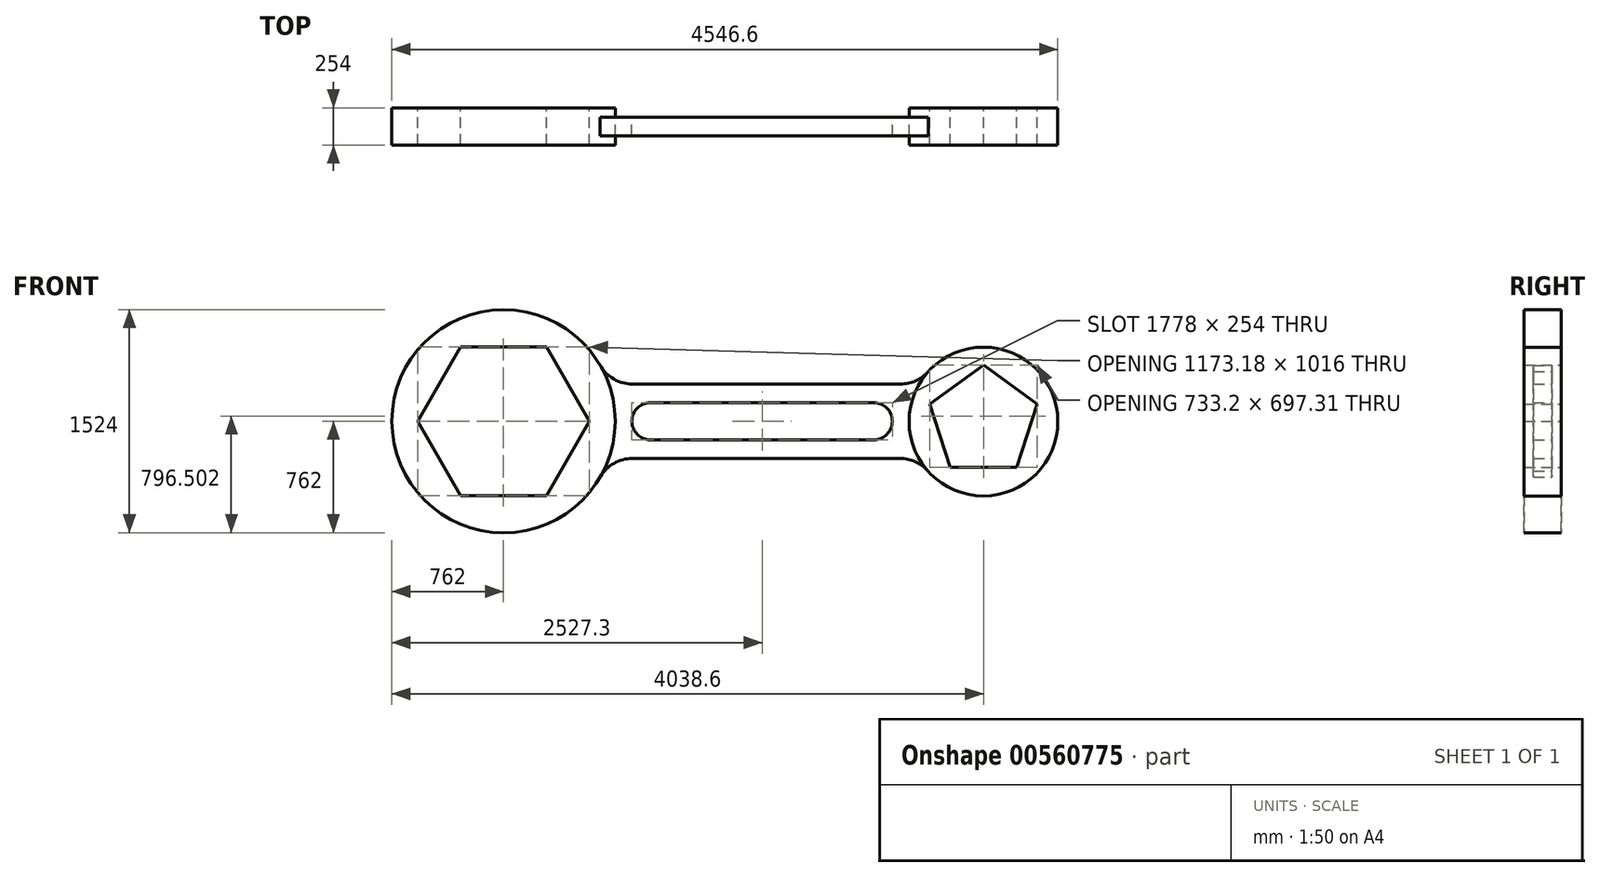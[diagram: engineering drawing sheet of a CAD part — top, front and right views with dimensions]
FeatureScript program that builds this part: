
annotation { "Feature Type Name" : "Feature", "Feature Type Description" : "" }
export const myFeature = defineFeature(function(context is Context, id is Id, definition is map)
    precondition{}
    {
        {
            var Q0;
            Q0=qCreatedBy(makeId("Front.planeOp"),FACE);
            var sketch = newSketch(context, id + "F0", { "sketchPlane" : qUnion([Q0])});
            skLineSegment(sketch, "E0", {"start": v(0, 0) * mm, "end": v(1524, 0) * mm});
            skLineSegment(sketch, "E1", {"start": v(0, 254) * mm, "end": v(1524, 254) * mm});
            skArc(sketch, "E2", {"start": v(0, 254) * mm, "mid": v(-127, 127) * mm, "end": v(0, 0) * mm});
            skArc(sketch, "E3", {"start": v(1524, 0) * mm, "mid": v(1651, 127) * mm, "end": v(1524, 254) * mm});
            skPoint(sketch, "E4.centerSnap0", {"position": v(1651, 127) * mm});
            skPoint(sketch, "E5.0.midPoint", {"position": v(-622.3, -127) * mm});
            skPoint(sketch, "E6.0.midPoint", {"position": v(2019.3, -63.5) * mm});
            skPoint(sketch, "E7.centerSnap0", {"position": v(-127, 127) * mm});
            skCircle(sketch, "E8", {"center": v(-1003.3, 127) * mm, "radius": 762 * mm});
            skLineSegment(sketch, "E9.0", {"start": v(-710, -381) * mm, "end": v(-1296.6, -381) * mm});
            skLineSegment(sketch, "E9.1", {"start": v(-1296.6, -381) * mm, "end": v(-1589.89, 127) * mm});
            skLineSegment(sketch, "E9.2", {"start": v(-1589.89, 127) * mm, "end": v(-1296.6, 635) * mm});
            skLineSegment(sketch, "E9.3", {"start": v(-1296.6, 635) * mm, "end": v(-710, 635) * mm});
            skLineSegment(sketch, "E9.4", {"start": v(-710, 635) * mm, "end": v(-416.71, 127) * mm});
            skLineSegment(sketch, "E9.5", {"start": v(-416.71, 127) * mm, "end": v(-710, -381) * mm});
            skPoint(sketch, "E9.0.midPoint", {"position": v(-1003.3, -381) * mm});
            skArc(sketch, "E10", {"start": v(2279.5, 505.64) * mm, "mid": v(2273.3, 505.7) * mm, "end": v(2267.08, 505.64) * mm});
            skLineSegment(sketch, "E11.0", {"start": v(2499.87, -187.15) * mm, "end": v(2046.73, -187.15) * mm});
            skLineSegment(sketch, "E11.1", {"start": v(2046.73, -187.15) * mm, "end": v(1906.7, 243.8) * mm});
            skLineSegment(sketch, "E11.2", {"start": v(1906.7, 243.8) * mm, "end": v(2273.3, 510.16) * mm});
            skLineSegment(sketch, "E11.3", {"start": v(2273.3, 510.16) * mm, "end": v(2639.9, 243.8) * mm});
            skLineSegment(sketch, "E11.4", {"start": v(2639.9, 243.8) * mm, "end": v(2499.87, -187.15) * mm});
            skPoint(sketch, "E11.0.midPoint", {"position": v(2273.3, -187.15) * mm});
            skArc(sketch, "E12.trimOffspring", {"start": v(1912.91, 248.32) * mm, "mid": v(1910.94, 242.43) * mm, "end": v(1909.07, 236.5) * mm});
            skArc(sketch, "E13.trimOffspring", {"start": v(2044.35, -179.85) * mm, "mid": v(2049.35, -183.54) * mm, "end": v(2054.4, -187.15) * mm});
            skArc(sketch, "E14.trimOffspring", {"start": v(2492.18, -187.15) * mm, "mid": v(2497.24, -183.54) * mm, "end": v(2502.24, -179.85) * mm});
            skArc(sketch, "E15.trimOffspring", {"start": v(2637.52, 236.5) * mm, "mid": v(2635.65, 242.43) * mm, "end": v(2633.68, 248.32) * mm});
            skPoint(sketch, "E16.start.orphan", {"position": v(0, -127) * mm});
            skPoint(sketch, "E17.start.orphan", {"position": v(0, 381) * mm});
            skLineSegment(sketch, "E18", {"start": v(-127, -127) * mm, "end": v(1651, -127) * mm});
            skLineSegment(sketch, "E19", {"start": v(-127, 381) * mm, "end": v(1651, 381) * mm});
            skArc(sketch, "E20", {"start": v(-123.42, -127) * mm, "mid": v(-250.42, -161.03) * mm, "end": v(-343.39, -254) * mm});
            skArc(sketch, "E21", {"start": v(-343.39, 508) * mm, "mid": v(-250.42, 415.03) * mm, "end": v(-123.42, 381) * mm});
            skCircle(sketch, "E22", {"center": v(2273.3, 124.7) * mm, "radius": 508 * mm});
            skArc(sketch, "E23", {"start": v(1893.29, -212.44) * mm, "mid": v(1807.44, -149.34) * mm, "end": v(1703.28, -127) * mm});
            skArc(sketch, "E24", {"start": v(1707.4, 381) * mm, "mid": v(1810.63, 402.92) * mm, "end": v(1896.04, 464.9) * mm});
            skLineSegment(sketch, "E25", {"start": v(1651, 381) * mm, "end": v(1707.4, 381) * mm});
            skLineSegment(sketch, "E26", {"start": v(1651, -127) * mm, "end": v(1703.28, -127) * mm});
            skLineSegment(sketch, "E27.trimOffspring", {"start": v(1834.7, 381) * mm, "end": v(1849.9, 381) * mm});
            skSolve(sketch);
        }
        {
            var Q0;
            Q0=makeQuery(id+"F0.imprint","IMPRINT",FACE,{"disambiguationData":[TD([[makeQuery(id+"F0.imprint","IMPRINT",EDGE,{"derivedFrom":sQuery(id+"F0.wireOp",EDGE,"E9.0")}),1.0]])]});
            var Q1;
            {var subQ18=sQuery(id+"F0.wireOp",EDGE,"E22");var subQ20=makeQuery(id+"F0.imprint","IMPRINT",VERTEX,{"derivedFrom":subQ18});Q1=makeQuery(id+"F0.imprint","IMPRINT",FACE,{"disambiguationData":[TD([[makeQuery(id+"F0.imprint","IMPRINT",EDGE,{"disambiguationData":[TD([[subQ20,1.0]])],"derivedFrom":subQ18}),1.0]])]});}
            extrude(context, id + "F1", {"entities" : qUnion([Q0, Q1]), "depth" : 254 * mm, "offsetDistance" : 25.4 * mm, "symmetric" : true});
        }
        {
            var Q0;
            Q0=makeQuery(id+"F0.imprint","IMPRINT",FACE,{"disambiguationData":[TD([[makeQuery(id+"F0.imprint","IMPRINT",EDGE,{"derivedFrom":sQuery(id+"F0.wireOp",EDGE,"E0")}),-1.0]])]});
            extrude(context, id + "F2", {"entities" : qUnion([Q0]), "depth" : 127 * mm, "offsetDistance" : 25.4 * mm, "symmetric" : true});
        }
    });
